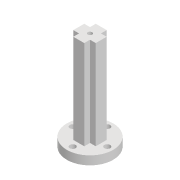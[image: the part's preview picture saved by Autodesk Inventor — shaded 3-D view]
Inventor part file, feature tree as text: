
AUTODESK INVENTOR PART (.ipt)
format: ipt  version: 2022 (Build 260153000, 153)  size: 142,336 bytes
history: native  units: mm
features: extrude x6, sketch x6, pattern_circular x1
ambient origin geometry x8: Origin, YZ Plane, XZ Plane, XY Plane, X Axis, Y Axis, Z Axis, Center Point
bodies: Solid1 (feature_tree)
feature tree (13):
  extrude  "Extrusion1"  Depth=3.0mm TaperAngle=0.0deg
  extrude  "Extrusion2"  Depth=2.0mm
  pattern_circular  "Circular Pattern1"  Count=4 Angle=360.0deg
  extrude  "Extrusion3"  Depth=7.8mm
  extrude  "Extrusion4"  Depth=2.0mm
  extrude  "Extrusion5"  Depth=3.0mm
  extrude  "Extrusion6"  Depth=8.0mm TaperAngle=0.0deg
  sketch  "Sketch1"  dims[d0=16.0mm d1=3.0mm d2=0.0mm]
  sketch  "Sketch2"  dims[d3=2.0mm d4=6.0mm]
  sketch  "Sketch3"  dims[d5=3.0mm d6=0.0mm d7=40.0mm d8=360.0deg]
  sketch  "Sketch4"  dims[d10=7.8mm d11=7.8mm]
  sketch  "Sketch5"  dims[d12=31.0mm d13=0.0mm d14=2.0mm]
  sketch  "Sketch6"  dims[d15=2.0mm d16=1.5mm d17=8.0mm d18=0.0mm d20=9.0mm d21=2.2mm d22=0.0mm d23=5.0mm d24=3.0mm d25=0.0mm]
